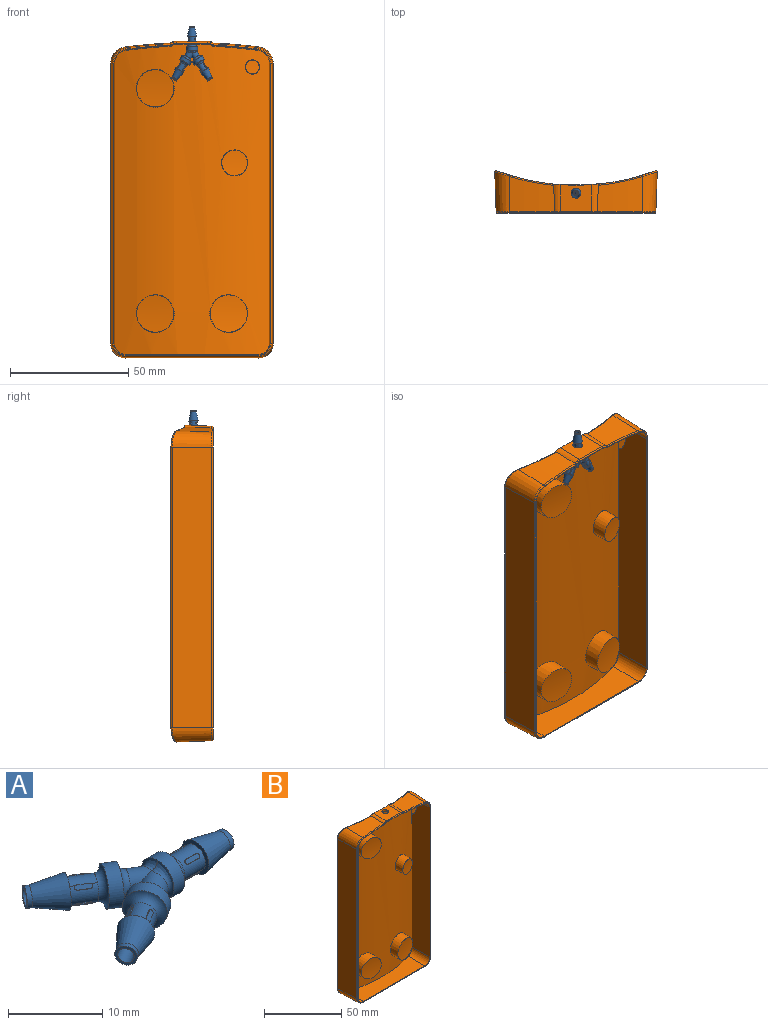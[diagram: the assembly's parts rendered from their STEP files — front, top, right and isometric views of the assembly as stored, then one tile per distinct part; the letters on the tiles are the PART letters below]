
ASSEMBLY  parts=2 mates=1
PART A: 90 faces, bbox 23.2x17.3x6.7 mm
  f0: bspline ~4.9x2.71mm, area 6.9mm2, adj f8,f10,f49
  f1: cylinder r=0.9mm len=13.28mm, axis (-0.85,0.52,0), area 79.5mm2, adj f9,f11,f50
  f2: cylinder r=1.53mm len=4.26mm, axis (0.85,-0.52,0), area 26.8mm2, adj f14,f17,f30,f31,f32,f33,f35,f36
  f3: cylinder r=1.53mm len=3.12mm, axis (-1,0,0), area 26.6mm2, adj f7,f18,f20,f21,f22,f23,f25,f26
  f4: plane 2.43x2.43mm, normal (1,0,0), area 2.1mm2, adj f5,f9
  f5: cylinder r=1.22mm len=2.43mm, axis (-1,0,0), area 4.4mm2, adj f4,f6
  f6: cone r=1.22mm half-angle=11.6deg, axis (-1,0,0), area 42.1mm2, adj f5,f7
  f7: plane 4.09x4.09mm, normal (-1,0,0), area 5.7mm2, adj f3,f6
  f8: cylinder r=2.45mm len=4.91mm, axis (-1,0,0), area 25.1mm2, adj f0,f18,f49
  f9: cylinder r=0.9mm len=10.27mm, axis (-1,0,0), area 58.2mm2, adj f1,f4,f50
  f10: cylinder r=1.53mm len=3.96mm, axis (-0.85,0.52,0), area 16.9mm2, adj f0,f16,f52
  f11: plane 2.43x2.07mm, normal (-0.85,0.52,0), area 2.1mm2, adj f1,f12
  f12: cylinder r=1.22mm len=2.43mm, axis (0.85,-0.52,0), area 4.4mm2, adj f11,f13
  f13: cone r=1.22mm half-angle=11.6deg, axis (0.85,-0.52,0), area 42.1mm2, adj f12,f14
  f14: plane 4.09x3.48mm, normal (0.85,-0.52,0), area 5.7mm2, adj f2,f13
  f15: cylinder r=2.45mm len=5.03mm, axis (0.85,-0.52,0), area 25.1mm2, adj f16,f17
  f16: torus R=2.45mm, axis (0.85,-0.52,0), area 17mm2, adj f10,f15
  f17: torus R=2.45mm, axis (0.85,-0.52,0), area 17mm2, adj f2,f15
  f18: torus R=2.45mm, axis (-1,0,0), area 17mm2, adj f3,f8
  f19: plane 2.08x0.41mm, normal (0,0.71,0.71), area 1.1mm2, adj f20,f21,f22,f23
  f20: plane 1.5x0.07mm, normal (0,0.71,-0.71), area 0.2mm2, adj f3,f19,f21,f23
  f21: cylinder r=0.29mm len=0.48mm, axis (0,-0.71,-0.71), area 0.1mm2, adj f3,f19,f20,f22
  f22: plane 1.5x0.07mm, normal (0,-0.71,0.71), area 0.2mm2, adj f3,f19,f21,f23
  f23: cylinder r=0.29mm len=0.48mm, axis (0,-0.71,-0.71), area 0.1mm2, adj f3,f19,f20,f22
  f24: plane 2.08x0.41mm, normal (0,0.71,-0.71), area 1.1mm2, adj f25,f26,f27,f28
  f25: plane 1.5x0.07mm, normal (0,0.71,0.71), area 0.2mm2, adj f3,f24,f26,f28
  f26: cylinder r=0.29mm len=0.48mm, axis (0,0.71,-0.71), area 0.1mm2, adj f3,f24,f25,f27
  f27: plane 1.5x0.07mm, normal (0,-0.71,-0.71), area 0.2mm2, adj f3,f24,f26,f28
  f28: cylinder r=0.29mm len=0.48mm, axis (0,0.71,-0.71), area 0.1mm2, adj f3,f24,f25,f27
  f29: plane 1.72x1.19mm, normal (0.37,0.6,0.71), area 1.1mm2, adj f30,f31,f32,f33
  f30: plane 1.23x0.79mm, normal (0.37,0.6,-0.71), area 0.1mm2, adj f2,f29,f31,f33
  f31: cylinder r=0.29mm len=0.48mm, axis (-0.37,-0.6,-0.71), area 0.1mm2, adj f2,f29,f30,f32
  f32: plane 1.23x0.79mm, normal (-0.37,-0.6,0.71), area 0.1mm2, adj f2,f29,f31,f33
  f33: cylinder r=0.29mm len=0.48mm, axis (-0.37,-0.6,-0.71), area 0.1mm2, adj f2,f29,f30,f32
  f34: plane 1.72x1.19mm, normal (-0.37,-0.6,-0.71), area 1.1mm2, adj f35,f36,f37,f38
  f35: plane 1.23x0.79mm, normal (0.37,0.6,-0.71), area 0.1mm2, adj f2,f34,f36,f38
  f36: cylinder r=0.29mm len=0.48mm, axis (-0.37,-0.6,-0.71), area 0.1mm2, adj f2,f34,f35,f37
  f37: plane 1.23x0.79mm, normal (-0.37,-0.6,0.71), area 0.1mm2, adj f2,f34,f36,f38
  f38: cylinder r=0.29mm len=0.48mm, axis (-0.37,-0.6,-0.71), area 0.1mm2, adj f2,f34,f35,f37
  f39: plane 1.72x1.19mm, normal (0.37,0.6,-0.71), area 1.1mm2, adj f40,f41,f42,f43
  f40: plane 1.23x0.79mm, normal (-0.37,-0.6,-0.71), area 0.1mm2, adj f2,f39,f41,f43
  f41: cylinder r=0.29mm len=0.48mm, axis (-0.37,-0.6,0.71), area 0.1mm2, adj f2,f39,f40,f42
  f42: plane 1.23x0.79mm, normal (0.37,0.6,0.71), area 0.1mm2, adj f2,f39,f41,f43
  f43: cylinder r=0.29mm len=0.48mm, axis (-0.37,-0.6,0.71), area 0.1mm2, adj f2,f39,f40,f42
  f44: cylinder r=0.29mm len=0.48mm, axis (-0.37,-0.6,0.71), area 0.1mm2, adj f2,f45,f47,f48
  f45: plane 1.23x0.79mm, normal (0.37,0.6,0.71), area 0.1mm2, adj f2,f44,f46,f48
  f46: cylinder r=0.29mm len=0.48mm, axis (-0.37,-0.6,0.71), area 0.1mm2, adj f2,f45,f47,f48
  f47: plane 1.23x0.79mm, normal (-0.37,-0.6,-0.71), area 0.1mm2, adj f2,f44,f46,f48
  f48: plane 1.72x1.19mm, normal (-0.37,-0.6,0.71), area 1.1mm2, adj f44,f45,f46,f47
  f49: bspline ~4.9x2.71mm, area 6.9mm2, adj f0,f8,f52
  f50: cylinder r=0.9mm len=13.28mm, axis (-0.85,-0.52,0), area 79.5mm2, adj f1,f9,f53
  f51: cylinder r=1.53mm len=4.26mm, axis (0.85,0.52,0), area 26.8mm2, adj f56,f59,f71,f72,f73,f74,f76,f77
  f52: cylinder r=1.53mm len=3.96mm, axis (-0.85,-0.52,0), area 16.9mm2, adj f10,f49,f58
  f53: plane 2.43x2.07mm, normal (-0.85,-0.52,0), area 2.1mm2, adj f50,f54
  f54: cylinder r=1.22mm len=2.43mm, axis (0.85,0.52,0), area 4.4mm2, adj f53,f55
  f55: cone r=1.22mm half-angle=11.6deg, axis (0.85,0.52,0), area 42.1mm2, adj f54,f56
  f56: plane 4.09x3.48mm, normal (0.85,0.52,0), area 5.7mm2, adj f51,f55
  f57: cylinder r=2.45mm len=5.03mm, axis (0.85,0.52,0), area 25.1mm2, adj f58,f59
  f58: torus R=2.45mm, axis (0.85,0.52,0), area 17mm2, adj f52,f57
  f59: torus R=2.45mm, axis (0.85,0.52,0), area 17mm2, adj f51,f57
  f60: plane 2.08x0.41mm, normal (0,-0.71,0.71), area 1.1mm2, adj f61,f62,f63,f64
  f61: plane 1.5x0.07mm, normal (0,-0.71,-0.71), area 0.2mm2, adj f3,f60,f62,f64
  f62: cylinder r=0.29mm len=0.48mm, axis (0,0.71,-0.71), area 0.1mm2, adj f3,f60,f61,f63
  f63: plane 1.5x0.07mm, normal (0,0.71,0.71), area 0.2mm2, adj f3,f60,f62,f64
  f64: cylinder r=0.29mm len=0.48mm, axis (0,0.71,-0.71), area 0.1mm2, adj f3,f60,f61,f63
  f65: plane 2.08x0.41mm, normal (0,-0.71,-0.71), area 1.1mm2, adj f66,f67,f68,f69
  f66: plane 1.5x0.07mm, normal (0,-0.71,0.71), area 0.2mm2, adj f3,f65,f67,f69
  f67: cylinder r=0.29mm len=0.48mm, axis (0,-0.71,-0.71), area 0.1mm2, adj f3,f65,f66,f68
  f68: plane 1.5x0.07mm, normal (0,0.71,-0.71), area 0.2mm2, adj f3,f65,f67,f69
  f69: cylinder r=0.29mm len=0.48mm, axis (0,-0.71,-0.71), area 0.1mm2, adj f3,f65,f66,f68
  f70: plane 1.72x1.19mm, normal (0.37,-0.6,0.71), area 1.1mm2, adj f71,f72,f73,f74
  f71: plane 1.23x0.79mm, normal (0.37,-0.6,-0.71), area 0.1mm2, adj f51,f70,f72,f74
  f72: cylinder r=0.29mm len=0.48mm, axis (-0.37,0.6,-0.71), area 0.1mm2, adj f51,f70,f71,f73
  f73: plane 1.23x0.79mm, normal (-0.37,0.6,0.71), area 0.1mm2, adj f51,f70,f72,f74
  f74: cylinder r=0.29mm len=0.48mm, axis (-0.37,0.6,-0.71), area 0.1mm2, adj f51,f70,f71,f73
  f75: plane 1.72x1.19mm, normal (-0.37,0.6,-0.71), area 1.1mm2, adj f76,f77,f78,f79
  f76: plane 1.23x0.79mm, normal (0.37,-0.6,-0.71), area 0.1mm2, adj f51,f75,f77,f79
  f77: cylinder r=0.29mm len=0.48mm, axis (-0.37,0.6,-0.71), area 0.1mm2, adj f51,f75,f76,f78
  f78: plane 1.23x0.79mm, normal (-0.37,0.6,0.71), area 0.1mm2, adj f51,f75,f77,f79
  f79: cylinder r=0.29mm len=0.48mm, axis (-0.37,0.6,-0.71), area 0.1mm2, adj f51,f75,f76,f78
  f80: plane 1.72x1.19mm, normal (0.37,-0.6,-0.71), area 1.1mm2, adj f81,f82,f83,f84
  f81: plane 1.23x0.79mm, normal (-0.37,0.6,-0.71), area 0.1mm2, adj f51,f80,f82,f84
  f82: cylinder r=0.29mm len=0.48mm, axis (-0.37,0.6,0.71), area 0.1mm2, adj f51,f80,f81,f83
  f83: plane 1.23x0.79mm, normal (0.37,-0.6,0.71), area 0.1mm2, adj f51,f80,f82,f84
  f84: cylinder r=0.29mm len=0.48mm, axis (-0.37,0.6,0.71), area 0.1mm2, adj f51,f80,f81,f83
  f85: cylinder r=0.29mm len=0.48mm, axis (-0.37,0.6,0.71), area 0.1mm2, adj f51,f86,f88,f89
  f86: plane 1.23x0.79mm, normal (0.37,-0.6,0.71), area 0.1mm2, adj f51,f85,f87,f89
  f87: cylinder r=0.29mm len=0.48mm, axis (-0.37,0.6,0.71), area 0.1mm2, adj f51,f86,f88,f89
  f88: plane 1.23x0.79mm, normal (-0.37,0.6,-0.71), area 0.1mm2, adj f51,f85,f87,f89
  f89: plane 1.72x1.19mm, normal (-0.37,0.6,0.71), area 1.1mm2, adj f85,f86,f87,f88
PART B: 69 faces, bbox 77.4x20x134.5 mm
  f0: cylinder r=96.1mm len=133.45mm, axis (0,0,1), area 8627.6mm2, adj f2,f3,f13,f49,f51,f53,f55,f57
  f1: cylinder r=96.1mm len=131.05mm, axis (0,0,-1), area 7895.6mm2, adj f27,f28,f29,f30,f31,f32,f33,f34
  f2: plane 13.93x11.82mm, normal (0,-0.03,1), area 138.6mm2, adj f0,f3,f13,f22,f68
  f3: cone r=4.17mm half-angle=2deg, axis (0,1,0), area 31.3mm2, adj f0,f2,f4,f24,f59
  f4: cone r=207.86mm half-angle=2deg, axis (0,1,0), area 245.9mm2, adj f3,f5,f26,f59
  f5: cone r=6.5mm half-angle=2deg, axis (0,1,0), area 154.1mm2, adj f4,f6,f25,f60
  f6: plane 118.55x16.77mm, normal (-1,-0.03,0), area 1988.9mm2, adj f5,f7,f23,f61
  f7: cone r=5.5mm half-angle=2deg, axis (0,1,0), area 144mm2, adj f6,f8,f21,f62
  f8: plane 56.5x14.86mm, normal (0,-0.03,-1), area 680.4mm2, adj f7,f9,f19,f63
  f9: cone r=5.5mm half-angle=2deg, axis (0,1,0), area 144mm2, adj f8,f10,f17,f64
  f10: plane 118.55x16.77mm, normal (1,-0.03,0), area 1988.9mm2, adj f9,f11,f15,f65
  f11: cone r=6.5mm half-angle=2deg, axis (0,1,0), area 154.1mm2, adj f10,f12,f16,f66
  f12: cone r=207.86mm half-angle=2deg, axis (0,1,0), area 245.9mm2, adj f11,f13,f18,f67
  f13: cone r=4.17mm half-angle=2deg, axis (0,1,0), area 31.3mm2, adj f0,f2,f12,f20,f67
  f14: plane 132.03x66.53mm, normal (0,-1,0), area 102.2mm2, adj f15,f16,f17,f18,f19,f20,f21,f22
  f15: cylinder r=0.5mm len=118.55mm, axis (0,0,1), area 91mm2, adj f10,f14,f16,f17
  f16: torus R=6.02mm, axis (0,-1,0), area 7mm2, adj f11,f14,f15,f18
  f17: torus R=5.02mm, axis (0,-1,0), area 6.4mm2, adj f9,f14,f15,f19
  f18: torus R=207.38mm, axis (0,-1,0), area 14.6mm2, adj f12,f14,f16,f20
  f19: cylinder r=0.5mm len=56.5mm, axis (1,0,0), area 43.4mm2, adj f8,f14,f17,f21
  f20: torus R=3.68mm, axis (0,-1,0), area 2mm2, adj f13,f14,f18,f22
  f21: torus R=5.02mm, axis (0,-1,0), area 6.4mm2, adj f7,f14,f19,f23
  f22: cylinder r=0.5mm len=13.5mm, axis (-1,0,0), area 10.4mm2, adj f2,f14,f20,f24
  f23: cylinder r=0.5mm len=118.55mm, axis (0,0,-1), area 91mm2, adj f6,f14,f21,f25
  f24: torus R=3.68mm, axis (0,-1,0), area 2mm2, adj f3,f14,f22,f26
  f25: torus R=6.02mm, axis (0,-1,0), area 7mm2, adj f5,f14,f23,f26
  f26: torus R=207.38mm, axis (0,-1,0), area 14.6mm2, adj f4,f14,f24,f25
  f27: cone r=5.75mm half-angle=1deg, axis (0,-1,0), area 125.6mm2, adj f1,f14,f28,f38
  f28: cone r=207.11mm half-angle=1deg, axis (0,-1,0), area 248.3mm2, adj f1,f14,f27,f29
  f29: cone r=3.42mm half-angle=1deg, axis (0,-1,0), area 25.6mm2, adj f1,f14,f28,f30
  f30: plane 13.51x10.89mm, normal (0,-0.02,-1), area 131.5mm2, adj f1,f14,f29,f31,f68
  f31: cone r=3.42mm half-angle=1deg, axis (0,-1,0), area 25.6mm2, adj f1,f14,f30,f32
  f32: cone r=207.11mm half-angle=1deg, axis (0,-1,0), area 248.3mm2, adj f1,f14,f31,f33
  f33: cone r=5.75mm half-angle=1deg, axis (0,-1,0), area 125.6mm2, adj f1,f14,f32,f34
  f34: plane 118.55x16.38mm, normal (1,-0.02,0), area 1942.1mm2, adj f1,f14,f33,f35
  f35: cone r=4.75mm half-angle=1deg, axis (0,-1,0), area 113.3mm2, adj f1,f14,f34,f36
  f36: plane 56.65x15.03mm, normal (0,-0.02,1), area 680.5mm2, adj f1,f14,f35,f37
  f37: cone r=4.75mm half-angle=1deg, axis (0,-1,0), area 113.3mm2, adj f1,f14,f36,f38
  f38: plane 118.55x16.38mm, normal (-1,-0.02,0), area 1942.1mm2, adj f1,f14,f27,f37
  f39: cylinder r=96.14mm len=15.77mm, axis (0,0,-1), area 197.6mm2, adj f40
  f40: cone r=7.5mm half-angle=1deg, axis (0,1,0), area 345mm2, adj f1,f39
  f41: cylinder r=96.14mm len=15.77mm, axis (0,0,-1), area 197.8mm2, adj f42
  f42: cone r=7.5mm half-angle=1deg, axis (0,1,0), area 343.5mm2, adj f1,f41
  f43: cylinder r=96.14mm len=15.77mm, axis (0,0,-1), area 197.8mm2, adj f44
  f44: cone r=7.5mm half-angle=1deg, axis (0,1,0), area 343.5mm2, adj f1,f43
  f45: cylinder r=96.14mm len=10.77mm, axis (0,0,-1), area 92.7mm2, adj f46
  f46: cone r=5mm half-angle=1deg, axis (0,1,0), area 236.7mm2, adj f1,f45
  f47: cylinder r=96.14mm len=5.83mm, axis (0,0,-1), area 27.6mm2, adj f48
  f48: cone r=2.5mm half-angle=1deg, axis (0,1,0), area 129.4mm2, adj f1,f47
  f49: cone r=6.5mm half-angle=1deg, axis (0,1,0), area 280.3mm2, adj f0,f50
  f50: cylinder r=96.14mm len=12.05mm, axis (0,0,-1), area 115.5mm2, adj f49
  f51: cone r=1.5mm half-angle=1deg, axis (0,1,0), area 47.8mm2, adj f0,f52
  f52: cylinder r=96.14mm len=2.12mm, axis (0,0,-1), area 3.6mm2, adj f51
  f53: cone r=4mm half-angle=1deg, axis (0,1,0), area 151.5mm2, adj f0,f54
  f54: cylinder r=96.14mm len=7.06mm, axis (0,0,-1), area 39.8mm2, adj f53
  f55: cone r=6.5mm half-angle=1deg, axis (0,1,0), area 254.4mm2, adj f0,f56
  f56: cylinder r=96.14mm len=12.05mm, axis (0,0,-1), area 115.5mm2, adj f55
  f57: cone r=6.5mm half-angle=1deg, axis (0,1,0), area 280.3mm2, adj f0,f58
  f58: cylinder r=96.14mm len=12.05mm, axis (0,0,-1), area 115.5mm2, adj f57
  f59: bspline ~35.09x8.4mm, area 15.3mm2, adj f0,f3,f4,f60
  f60: bspline ~8.61x7.94mm, area 9.3mm2, adj f0,f5,f59,f61
  f61: cylinder r=0.5mm len=118.55mm, axis (0,0,1), area 116.4mm2, adj f0,f6,f60,f62
  f62: bspline ~7.64x7.41mm, area 8.7mm2, adj f0,f7,f61,f63
  f63: bspline ~56.5x4.72mm, area 45.9mm2, adj f0,f8,f62,f64
  f64: bspline ~7.64x7.41mm, area 8.7mm2, adj f0,f9,f63,f65
  f65: cylinder r=0.5mm len=118.55mm, axis (0,0,1), area 116.4mm2, adj f0,f10,f64,f66
  f66: bspline ~8.61x7.94mm, area 9.3mm2, adj f0,f11,f65,f67
  f67: bspline ~35.09x8.4mm, area 15.3mm2, adj f0,f12,f13,f66
  f68: cylinder r=2.05mm len=4.12mm, axis (0,-0.02,-1), area 13.8mm2, adj f2,f30
PLACE A rot(axis=(0.57,-0.57,0.58),119.4deg) t=(0.37,-0.74,62.66)mm
PLACE B t=(-32.38,-0.38,-65.9)mm
MATE fastened A.f3 <-> B.f68  axis (0,-0.02,-1) through (0.37,-0.7,65.21)mm
